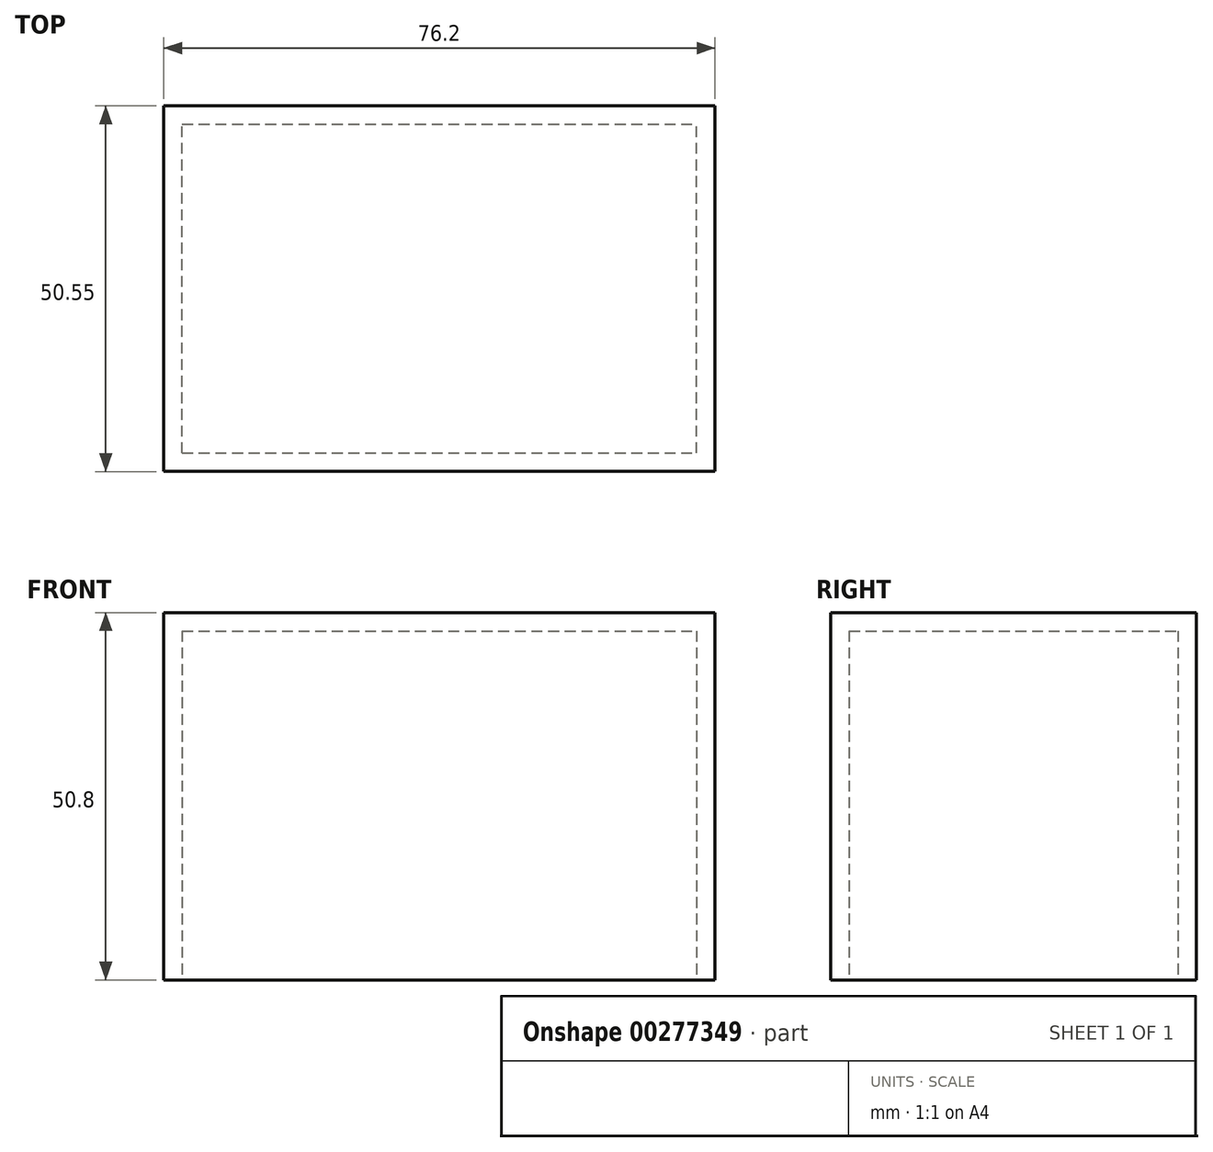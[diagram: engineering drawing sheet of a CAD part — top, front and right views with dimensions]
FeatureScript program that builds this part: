
annotation { "Feature Type Name" : "Feature", "Feature Type Description" : "" }
export const myFeature = defineFeature(function(context is Context, id is Id, definition is map)
    precondition{}
    {
        {
            var Q0;
            Q0=qCreatedBy(makeId("Front.planeOp"),FACE);
            var sketch = newSketch(context, id + "F0", { "sketchPlane" : qUnion([Q0])});
            skLineSegment(sketch, "E0.bottom", {"start": v(-31.46, 22.17) * mm, "end": v(44.74, 22.17) * mm});
            skLineSegment(sketch, "E0.top", {"start": v(-31.46, -28.63) * mm, "end": v(44.74, -28.63) * mm});
            skLineSegment(sketch, "E0.left", {"start": v(-31.46, 22.17) * mm, "end": v(-31.46, -28.63) * mm});
            skLineSegment(sketch, "E0.right", {"start": v(44.74, 22.17) * mm, "end": v(44.74, -28.63) * mm});
            skSolve(sketch);
        }
        {
            var Q0;
            Q0=makeQuery(id+"F0.imprint","IMPRINT",FACE,{"disambiguationData":[TD([[makeQuery(id+"F0.imprint","IMPRINT",EDGE,{"derivedFrom":sQuery(id+"F0.wireOp",EDGE,"E0.bottom")}),-1.0]])]});
            extrude(context, id + "F1", {"entities" : qUnion([Q0]), "depth" : 50.55 * mm});
        }
        {
            var Q0;
            Q0=makeQuery(id+"F1.opExtrude","SWEPT_FACE",FACE,{"disambiguationData":[OSD([sQuery(id+"F0.wireOp",EDGE,"E0.top")])]});
            shell(context, id + "F2", {"entities" : qUnion([Q0]), "thickness" : 2.54 * mm});
        }
    });
